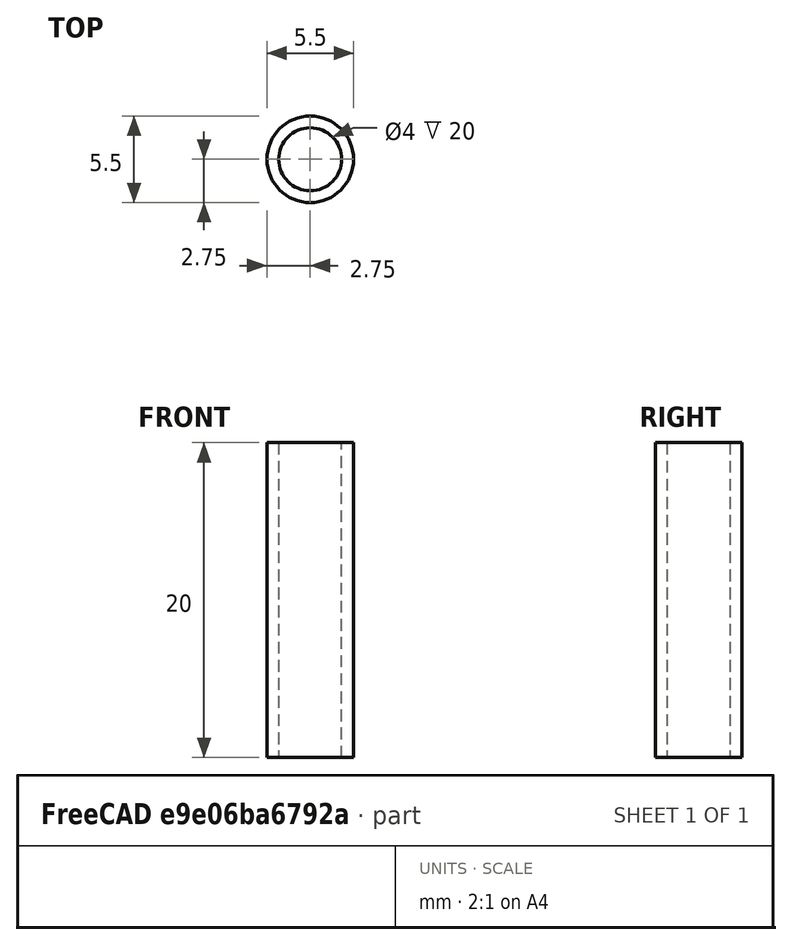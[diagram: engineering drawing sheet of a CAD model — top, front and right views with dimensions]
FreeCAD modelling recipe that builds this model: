
FCSTD DOCUMENT  (FreeCAD 0.18R16146 (Git))
Label: cigarette_filter
License: All rights reserved
LicenseURL: http://en.wikipedia.org/wiki/All_rights_reserved
objects: Sketcher::SketchObject×1, PartDesign::Pad×1, PartDesign::Body×1, App::MeasureDistance×1
note: 4 computed .brp shape members not serialized (recipe doc carries the construction recipe); baked Part::Feature solids carry a one-line shape summary decoded from their .brp

FEATURE [Sketcher::SketchObject] Sketch
  MapMode = 5
  Support = -> [XY_Plane]
  sketch-geometry (2):
    g0: Circle CenterX=0 CenterY=0 CenterZ=0 NormalX=0 NormalY=0 NormalZ=1 AngleXU=0 Radius=2.75
    g1: Circle CenterX=0 CenterY=0 CenterZ=0 NormalX=0 NormalY=0 NormalZ=1 AngleXU=0 Radius=2
  constraints (4):
    c: Radius(g0) = 2.75
    c: Coincident(g0,g-1)
    c: Coincident(g1,g0)
    c: Radius(g1) = 2
FEATURE [PartDesign::Pad] Pad
  Length = 20
  Length2 = 100
  Profile = -> Sketch
  Type = 0
FEATURE [PartDesign::Body] Body
  Group = -> [Sketch,Pad]
  Origin = -> Origin
  Tip = -> Pad
FEATURE [App::MeasureDistance] Distance  label="Distance: 4.48 mm"
  Distance = 4.48035
  P1 = (-1.79734,-1.32804,20)
  P2 = (1.68415,1.49203,20)
